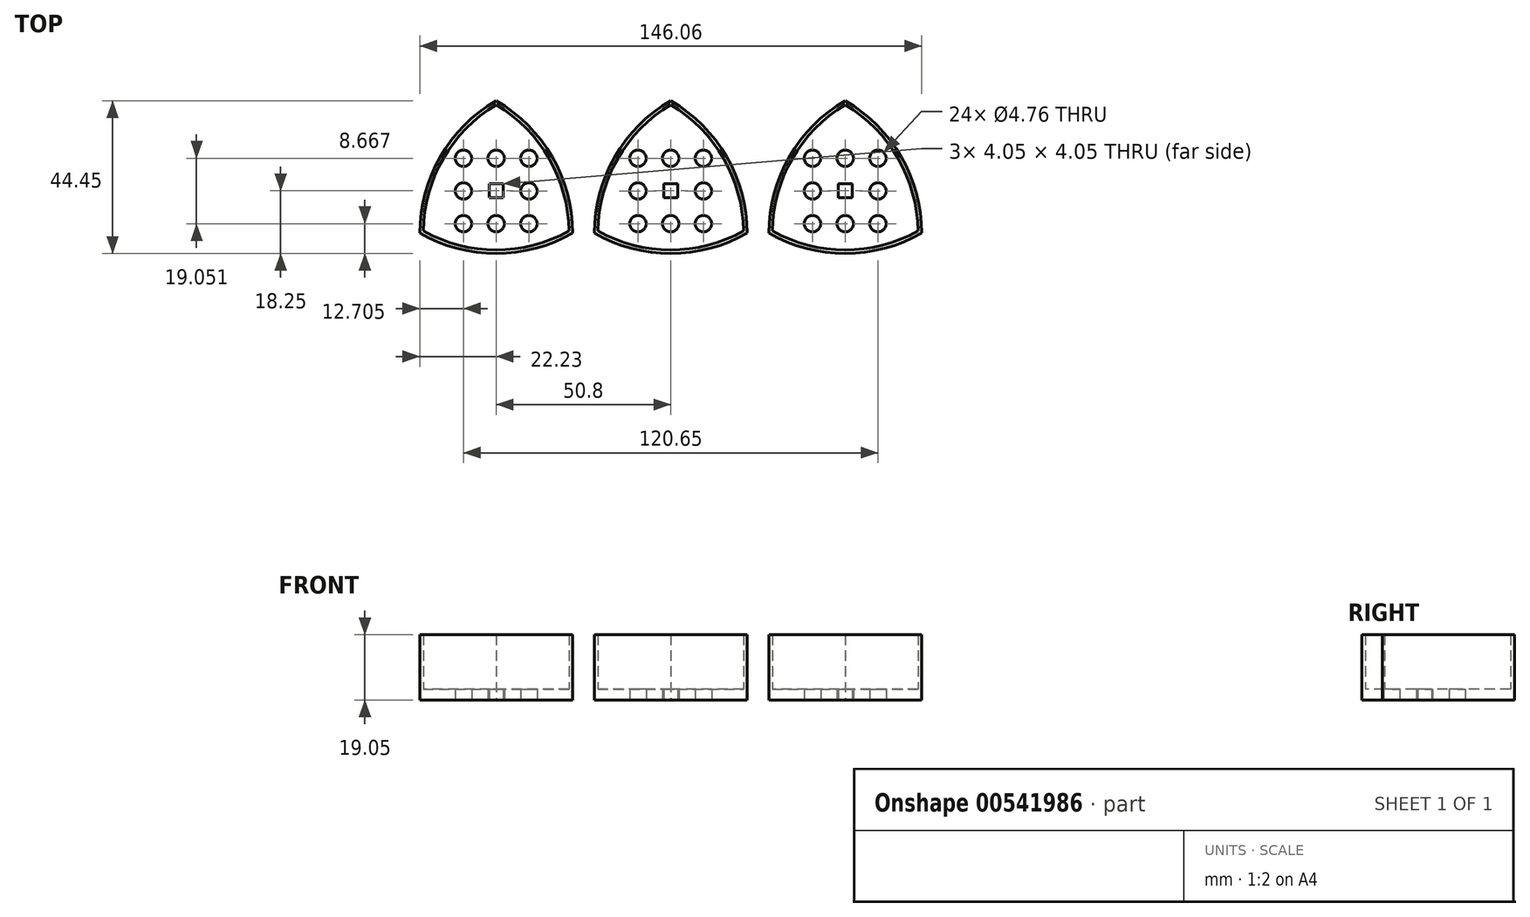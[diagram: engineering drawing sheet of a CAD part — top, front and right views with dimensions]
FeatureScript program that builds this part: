
annotation { "Feature Type Name" : "Feature", "Feature Type Description" : "" }
export const myFeature = defineFeature(function(context is Context, id is Id, definition is map)
    precondition{}
    {
        {
            var Q0;
            Q0=qCreatedBy(makeId("Top.planeOp"),FACE);
            var sketch = newSketch(context, id + "F0", { "sketchPlane" : qUnion([Q0])});
            skArc(sketch, "E0", {"start": v(22.22, -12.3) * mm, "mid": v(16.27, 9.93) * mm, "end": v(0, 26.2) * mm});
            skLineSegment(sketch, "E1", {"start": v(22.22, -12.3) * mm, "end": v(22.22, -12.3) * mm});
            skArc(sketch, "E2", {"start": v(0, 26.2) * mm, "mid": v(-16.27, 9.93) * mm, "end": v(-22.22, -12.3) * mm});
            skArc(sketch, "E3", {"start": v(-22.22, -12.3) * mm, "mid": v(0, -18.25) * mm, "end": v(22.23, -12.3) * mm});
            skLineSegment(sketch, "E4.bottom", {"start": v(-2.03, 2.03) * mm, "end": v(2.03, 2.03) * mm});
            skLineSegment(sketch, "E4.top", {"start": v(-2.03, -2.03) * mm, "end": v(2.03, -2.03) * mm});
            skLineSegment(sketch, "E4.left", {"start": v(2.03, 2.03) * mm, "end": v(2.03, -2.03) * mm});
            skLineSegment(sketch, "E4.right", {"start": v(-2.03, 2.03) * mm, "end": v(-2.03, -2.03) * mm});
            skPoint(sketch, "E4.middle", {"position": v(0, 0) * mm});
            skArc(sketch, "E5.0", {"start": v(-21.2, -11.7) * mm, "mid": v(0, -17.24) * mm, "end": v(21.2, -11.7) * mm});
            skArc(sketch, "E5.1", {"start": v(0, 25.02) * mm, "mid": v(-15.39, 9.42) * mm, "end": v(-21.2, -11.7) * mm});
            skArc(sketch, "E5.2", {"start": v(21.2, -11.7) * mm, "mid": v(15.39, 9.42) * mm, "end": v(0, 25.02) * mm});
            skSolve(sketch);
        }
        {
            var Q0;
            Q0=qCreatedBy(makeId("Top.planeOp"),FACE);
            var sketch = newSketch(context, id + "F1", { "sketchPlane" : qUnion([Q0])});
            skCircle(sketch, "E6", {"center": v(0, 9.47) * mm, "radius": 2.38 * mm});
            skCircle(sketch, "E7", {"center": v(-9.53, 9.47) * mm, "radius": 2.38 * mm});
            skCircle(sketch, "E8", {"center": v(9.53, -0.06) * mm, "radius": 2.38 * mm});
            skCircle(sketch, "E9", {"center": v(9.53, -9.58) * mm, "radius": 2.38 * mm});
            skCircle(sketch, "E10", {"center": v(0, -9.58) * mm, "radius": 2.38 * mm});
            skCircle(sketch, "E11", {"center": v(-9.53, -9.58) * mm, "radius": 2.38 * mm});
            skCircle(sketch, "E12", {"center": v(-9.52, -0.06) * mm, "radius": 2.38 * mm});
            skCircle(sketch, "E13.0", {"center": v(9.53, 9.47) * mm, "radius": 2.38 * mm});
            skCircle(sketch, "E14.0", {"center": v(9.53, 9.47) * mm, "radius": 3.97 * mm});
            skCircle(sketch, "E15.0", {"center": v(0, 9.47) * mm, "radius": 3.97 * mm});
            skCircle(sketch, "E16.0", {"center": v(-9.53, 9.47) * mm, "radius": 3.97 * mm});
            skCircle(sketch, "E17.0", {"center": v(-9.52, -0.06) * mm, "radius": 3.97 * mm});
            skCircle(sketch, "E18.0", {"center": v(-9.53, -9.58) * mm, "radius": 3.97 * mm});
            skCircle(sketch, "E19.0", {"center": v(0, -9.58) * mm, "radius": 3.97 * mm});
            skCircle(sketch, "E20.0", {"center": v(9.53, -9.58) * mm, "radius": 3.97 * mm});
            skCircle(sketch, "E21.0", {"center": v(9.53, -0.06) * mm, "radius": 3.97 * mm});
            skPoint(sketch, "E22", {"position": v(22.5, 15.34) * mm});
            skPoint(sketch, "E23", {"position": v(0, -0.06) * mm});
            skCircle(sketch, "E24.0", {"center": v(0, 0) * mm, "radius": 3.97 * mm});
            skSolve(sketch);
        }
        {
            var Q0;
            Q0=makeQuery(id+"F0.imprint","IMPRINT",FACE,{"disambiguationData":[TD([[makeQuery(id+"F0.imprint","IMPRINT",EDGE,{"derivedFrom":sQuery(id+"F0.wireOp",EDGE,"E0")}),1.0]])]});
            extrude(context, id + "F2", {"entities" : qUnion([Q0]), "depth" : 9.52 * mm, "offsetDistance" : 25.4 * mm});
        }
        {
            var Q0;
            Q0=makeQuery(id+"F0.imprint","IMPRINT",FACE,{"disambiguationData":[TD([[makeQuery(id+"F0.imprint","IMPRINT",EDGE,{"derivedFrom":sQuery(id+"F0.wireOp",EDGE,"E4.bottom")}),1.0]])]});
            extrude(context, id + "F3", {"entities" : qUnion([Q0]), "operationType" : NewBodyOperationType.ADD, "depth" : 3.17 * mm, "offsetDistance" : 25.4 * mm});
        }
        {
            var Q0;
            Q0=sQuery(id+"F1.wireOp",VERTEX,"E8.center");
            var Q1;
            Q1=sQuery(id+"F1.wireOp",VERTEX,"E9.center");
            var Q2;
            Q2=sQuery(id+"F1.wireOp",VERTEX,"E10.center");
            var Q3;
            Q3=sQuery(id+"F1.wireOp",VERTEX,"E11.center");
            var Q4;
            Q4=sQuery(id+"F1.wireOp",VERTEX,"E12.center");
            var Q5;
            Q5=sQuery(id+"F1.wireOp",VERTEX,"E7.center");
            var Q6;
            Q6=sQuery(id+"F1.wireOp",VERTEX,"E6.center");
            var Q7;
            Q7=sQuery(id+"F1.wireOp",VERTEX,"E13.0.center");
            var Q8;
            Q8=makeQuery(id+"F2.opExtrude","SWEPT_BODY",BODY,{"disambiguationData":[OSD([sQuery(id+"F0.wireOp",EDGE,"E0"),sQuery(id+"F0.wireOp",EDGE,"E2"),sQuery(id+"F0.wireOp",EDGE,"E3"),sQuery(id+"F0.wireOp",EDGE,"E5.0"),sQuery(id+"F0.wireOp",EDGE,"E5.1"),sQuery(id+"F0.wireOp",EDGE,"E5.2")])]});
            hole(context, id + "F4", {"style" : HoleStyle.SIMPLE, "endStyle" : HoleEndStyle.THROUGH, "oppositeDirection" : true, "holeDiameter" : 4.76 * mm, "isTappedThrough" : true, "tappedDepth" : 12.7 * mm, "tapClearance" : 3, "locations" : qUnion([Q0, Q1, Q2, Q3, Q4, Q5, Q6, Q7]), "scope" : qUnion([Q8])});
        }
        {
            var Q0;
            Q0=makeQuery(id+"F2.opExtrude","CAP_FACE",FACE,{"disambiguationData":[OSD([sQuery(id+"F0.wireOp",EDGE,"E0"),sQuery(id+"F0.wireOp",EDGE,"E2"),sQuery(id+"F0.wireOp",EDGE,"E3"),sQuery(id+"F0.wireOp",EDGE,"E5.0"),sQuery(id+"F0.wireOp",EDGE,"E5.1"),sQuery(id+"F0.wireOp",EDGE,"E5.2")])],"isStart":false});
            extrude(context, id + "F5", {"entities" : qUnion([Q0]), "operationType" : NewBodyOperationType.ADD, "depth" : 9.52 * mm, "offsetDistance" : 25.4 * mm});
        }
        {
            var Q0;
            Q0=qCreatedBy(makeId("Right.planeOp"),FACE);
            cPlane(context, id + "F6", {"entities" : qUnion([Q0]), "cplaneType" : CPlaneType.OFFSET, "offset" : 25.4 * mm, "width" : 152.4 * mm, "height" : 152.4 * mm});
        }
        {
            var Q0;
            Q0=makeQuery(id+"FKXasOYA6UBLgSY_1.opPattern","COPY",BODY,{"derivedFrom":makeQuery(id+"F2.opExtrude","SWEPT_BODY",BODY,{"disambiguationData":[OSD([sQuery(id+"F0.wireOp",EDGE,"E0"),sQuery(id+"F0.wireOp",EDGE,"E2"),sQuery(id+"F0.wireOp",EDGE,"E3"),sQuery(id+"F0.wireOp",EDGE,"E5.0"),sQuery(id+"F0.wireOp",EDGE,"E5.1"),sQuery(id+"F0.wireOp",EDGE,"E5.2")])]}),"instanceName":"1"});
            var Q1;
            Q1=makeQuery(id+"F2.opExtrude","SWEPT_BODY",BODY,{"disambiguationData":[OSD([sQuery(id+"F0.wireOp",EDGE,"E0"),sQuery(id+"F0.wireOp",EDGE,"E2"),sQuery(id+"F0.wireOp",EDGE,"E3"),sQuery(id+"F0.wireOp",EDGE,"E5.0"),sQuery(id+"F0.wireOp",EDGE,"E5.1"),sQuery(id+"F0.wireOp",EDGE,"E5.2")])]});
            var Q2;
            Q2=qCreatedBy(id+"F6.planeOp",FACE);
            mirror(context, id + "F7", {"entities" : qUnion([Q0, Q1]), "mirrorPlane" : qUnion([Q2])});
        }
        {
            var Q0;
            Q0=qCreatedBy(makeId("Right.planeOp"),FACE);
            cPlane(context, id + "F8", {"entities" : qUnion([Q0]), "cplaneType" : CPlaneType.OFFSET, "offset" : 25.4 * mm, "oppositeDirection" : true, "width" : 152.4 * mm, "height" : 152.4 * mm});
        }
        {
            var Q0;
            Q0=makeQuery(id+"F2.opExtrude","SWEPT_BODY",BODY,{"disambiguationData":[OSD([sQuery(id+"F0.wireOp",EDGE,"E0"),sQuery(id+"F0.wireOp",EDGE,"E2"),sQuery(id+"F0.wireOp",EDGE,"E3"),sQuery(id+"F0.wireOp",EDGE,"E5.0"),sQuery(id+"F0.wireOp",EDGE,"E5.1"),sQuery(id+"F0.wireOp",EDGE,"E5.2")])]});
            var Q1;
            Q1=qCreatedBy(id+"F8.planeOp",FACE);
            mirror(context, id + "F9", {"entities" : qUnion([Q0]), "mirrorPlane" : qUnion([Q1])});
        }
    });
